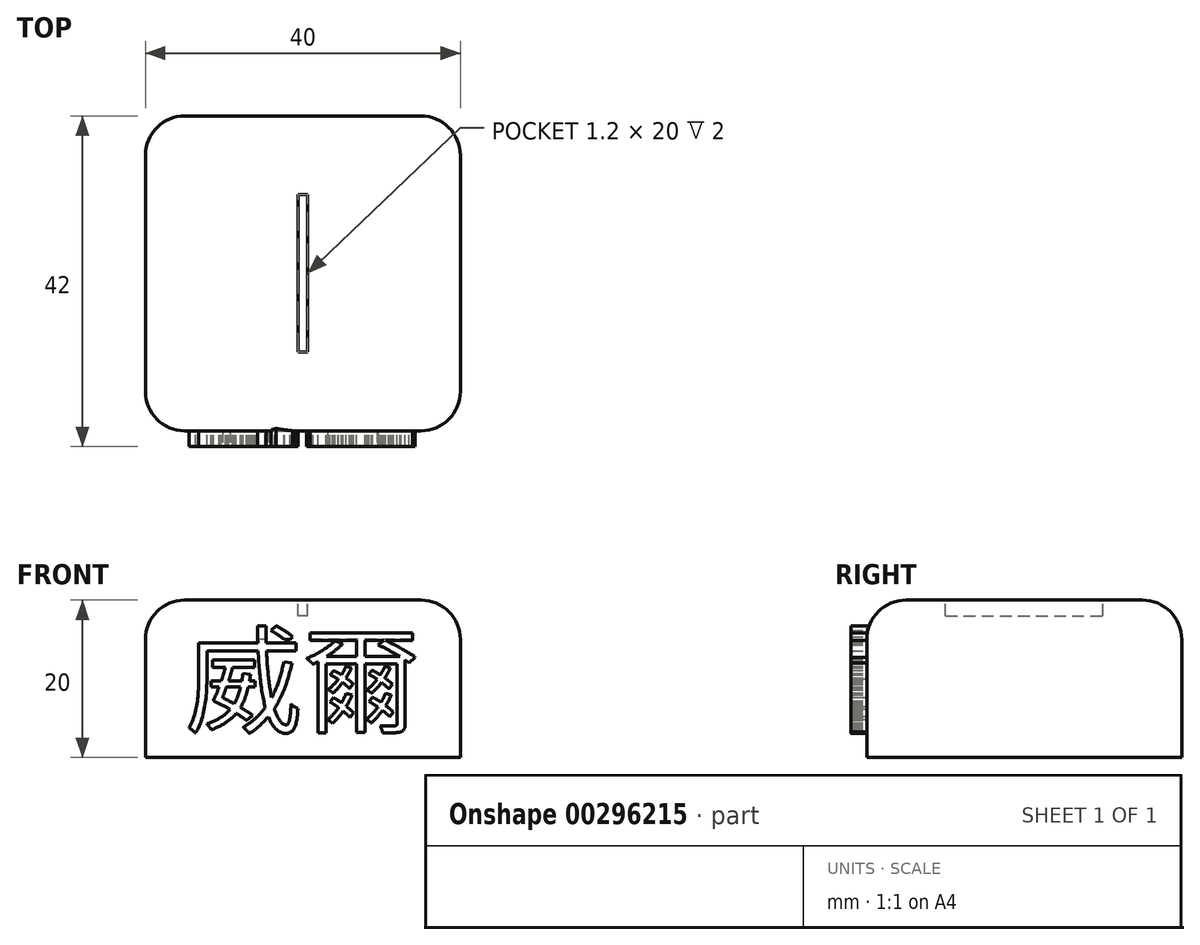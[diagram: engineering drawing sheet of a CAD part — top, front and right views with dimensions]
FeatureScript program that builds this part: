
annotation { "Feature Type Name" : "Feature", "Feature Type Description" : "" }
export const myFeature = defineFeature(function(context is Context, id is Id, definition is map)
    precondition{}
    {
        {
            var Q0;
            Q0=qCreatedBy(makeId("Top.planeOp"),FACE);
            var sketch = newSketch(context, id + "F0", { "sketchPlane" : qUnion([Q0])});
            skLineSegment(sketch, "E0.bottom", {"start": v(20, -20) * mm, "end": v(-20, -20) * mm});
            skLineSegment(sketch, "E0.top", {"start": v(20, 20) * mm, "end": v(-20, 20) * mm});
            skLineSegment(sketch, "E0.left", {"start": v(20, -20) * mm, "end": v(20, 20) * mm});
            skLineSegment(sketch, "E0.right", {"start": v(-20, -20) * mm, "end": v(-20, 20) * mm});
            skPoint(sketch, "E0.middle", {"position": v(0, 0) * mm});
            skLineSegment(sketch, "E1.bottom", {"start": v(0.6, -10) * mm, "end": v(-0.6, -10) * mm});
            skLineSegment(sketch, "E1.top", {"start": v(0.6, 10) * mm, "end": v(-0.6, 10) * mm});
            skLineSegment(sketch, "E1.left", {"start": v(0.6, -10) * mm, "end": v(0.6, 10) * mm});
            skLineSegment(sketch, "E1.right", {"start": v(-0.6, -10) * mm, "end": v(-0.6, 10) * mm});
            skSolve(sketch);
        }
        {
            var Q0;
            Q0=makeQuery(id+"F0.imprint","IMPRINT",FACE,{"disambiguationData":[TD([[makeQuery(id+"F0.imprint","IMPRINT",EDGE,{"derivedFrom":sQuery(id+"F0.wireOp",EDGE,"E0.bottom")}),-1.0]])]});
            var Q1;
            Q1=makeQuery(id+"F0.imprint","IMPRINT",FACE,{"disambiguationData":[TD([[makeQuery(id+"F0.imprint","IMPRINT",EDGE,{"derivedFrom":sQuery(id+"F0.wireOp",EDGE,"E1.bottom")}),-1.0]])]});
            extrude(context, id + "F1", {"entities" : qUnion([Q0, Q1]), "oppositeDirection" : true, "depth" : 20 * mm});
        }
        {
            var Q0;
            Q0=makeQuery(id+"F0.imprint","IMPRINT",FACE,{"disambiguationData":[TD([[makeQuery(id+"F0.imprint","IMPRINT",EDGE,{"derivedFrom":sQuery(id+"F0.wireOp",EDGE,"E1.bottom")}),-1.0]])]});
            extrude(context, id + "F2", {"entities" : qUnion([Q0]), "operationType" : NewBodyOperationType.REMOVE, "oppositeDirection" : true, "depth" : 2 * mm});
        }
        {
            var Q0;
            Q0=makeQuery(id+"F2.boolean.opBoolean","COPY",EDGE,{"derivedFrom":makeQuery(id+"F2.opExtrude","CAP_EDGE",EDGE,{"disambiguationData":[OSD([sQuery(id+"F0.wireOp",EDGE,"E1.left")])],"isStart":true})});
            var Q1;
            Q1=makeQuery(id+"F2.boolean.opBoolean","COPY",EDGE,{"derivedFrom":makeQuery(id+"F2.opExtrude","CAP_EDGE",EDGE,{"disambiguationData":[OSD([sQuery(id+"F0.wireOp",EDGE,"E1.right")])],"isStart":true})});
            var Q2;
            Q2=makeQuery(id+"F1.opExtrude","SWEPT_EDGE",EDGE,{"disambiguationData":[OSD([sQuery(id+"F0.wireOp",EDGE,"E0.bottom"),sQuery(id+"F0.wireOp",EDGE,"E0.left")])]});
            var Q3;
            Q3=makeQuery(id+"F1.opExtrude","SWEPT_EDGE",EDGE,{"disambiguationData":[OSD([sQuery(id+"F0.wireOp",EDGE,"E0.top"),sQuery(id+"F0.wireOp",EDGE,"E0.left")])]});
            var Q4;
            Q4=makeQuery(id+"F1.opExtrude","CAP_EDGE",EDGE,{"disambiguationData":[OSD([sQuery(id+"F0.wireOp",EDGE,"E0.left")])],"isStart":true});
            var Q5;
            Q5=makeQuery(id+"F1.opExtrude","SWEPT_EDGE",EDGE,{"disambiguationData":[OSD([sQuery(id+"F0.wireOp",EDGE,"E0.bottom"),sQuery(id+"F0.wireOp",EDGE,"E0.right")])]});
            var Q6;
            Q6=makeQuery(id+"F1.opExtrude","SWEPT_EDGE",EDGE,{"disambiguationData":[OSD([sQuery(id+"F0.wireOp",EDGE,"E0.top"),sQuery(id+"F0.wireOp",EDGE,"E0.right")])]});
            var Q7;
            Q7=makeQuery(id+"F1.opExtrude","CAP_EDGE",EDGE,{"disambiguationData":[OSD([sQuery(id+"F0.wireOp",EDGE,"E0.top")])],"isStart":true});
            var Q8;
            Q8=makeQuery(id+"F1.opExtrude","CAP_EDGE",EDGE,{"disambiguationData":[OSD([sQuery(id+"F0.wireOp",EDGE,"E0.right")])],"isStart":true});
            var Q9;
            Q9=makeQuery(id+"F1.opExtrude","CAP_EDGE",EDGE,{"disambiguationData":[OSD([sQuery(id+"F0.wireOp",EDGE,"E0.bottom")])],"isStart":true});
            fillet(context, id + "F3", {"entities" : qUnion([Q0, Q1, Q2, Q3, Q4, Q5, Q6, Q7, Q8, Q9]), "radius" : 5 * mm, "tangentPropagation" : true, "allowEdgeOverflow" : false});
        }
        {
            var Q0;
            Q0=makeQuery(id+"F1.opExtrude","SWEPT_FACE",FACE,{"disambiguationData":[OSD([sQuery(id+"F0.wireOp",EDGE,"E0.bottom")])]});
            var sketch = newSketch(context, id + "F4", { "sketchPlane" : qUnion([Q0])});
            skText(sketch, "E2", { "text": "威爾", "fontName": "NotoSansCJKtc-Regular.otf"});
            const initialGuessF4  = {"E2": [-0.015, -0.01575, 1, 0, 0.01075]};
            skSetInitialGuess(sketch, initialGuessF4);
            skSolve(sketch);
        }
        {
            var Q0;
            Q0=makeQuery(id+"F4.imprint","IMPRINT",FACE,{"disambiguationData":[TD([[makeQuery(id+"F4.imprint","IMPRINT",EDGE,{"derivedFrom":sQuery(id+"F4.wireOp",EDGE,"E2.sketch_text.stroke-34")}),1.0]])]});
            var Q1;
            {var subQ0=sQuery(id+"F4.wireOp",EDGE,"E2.sketch_text.stroke-40");Q1=makeQuery(id+"F4.imprint","IMPRINT",FACE,{"disambiguationData":[TD([[makeQuery(id+"F4.imprint","IMPRINT",EDGE,{"derivedFrom":subQ0}),1.0]])]});}
            var Q2;
            {var subQ7=sQuery(id+"F4.wireOp",EDGE,"E2.sketch_text.stroke-0");Q2=makeQuery(id+"F4.imprint","IMPRINT",FACE,{"disambiguationData":[TD([[makeQuery(id+"F4.imprint","IMPRINT",EDGE,{"derivedFrom":subQ7}),1.0]])]});}
            var Q3;
            Q3=makeQuery(id+"F4.imprint","IMPRINT",FACE,{"disambiguationData":[TD([[makeQuery(id+"F4.imprint","IMPRINT",EDGE,{"derivedFrom":sQuery(id+"F4.wireOp",EDGE,"E2.sketch_text.stroke-4")}),1.0]])]});
            var Q4;
            {var subQ0=sQuery(id+"F4.wireOp",EDGE,"E2.sketch_text.stroke-116");Q4=makeQuery(id+"F4.imprint","IMPRINT",FACE,{"disambiguationData":[TD([[makeQuery(id+"F4.imprint","IMPRINT",EDGE,{"derivedFrom":subQ0}),1.0]])]});}
            var Q5;
            Q5=makeQuery(id+"F4.imprint","IMPRINT",FACE,{"disambiguationData":[TD([[makeQuery(id+"F4.imprint","IMPRINT",EDGE,{"derivedFrom":sQuery(id+"F4.wireOp",EDGE,"E2.sketch_text.stroke-108")}),1.0]])]});
            var Q6;
            Q6=makeQuery(id+"F4.imprint","IMPRINT",FACE,{"disambiguationData":[TD([[makeQuery(id+"F4.imprint","IMPRINT",EDGE,{"derivedFrom":sQuery(id+"F4.wireOp",EDGE,"E2.sketch_text.stroke-72")}),1.0]])]});
            var Q7;
            Q7=makeQuery(id+"F4.imprint","IMPRINT",FACE,{"disambiguationData":[TD([[makeQuery(id+"F4.imprint","IMPRINT",EDGE,{"derivedFrom":sQuery(id+"F4.wireOp",EDGE,"E2.sketch_text.stroke-96")}),1.0]])]});
            var Q8;
            Q8=makeQuery(id+"F4.imprint","IMPRINT",FACE,{"disambiguationData":[TD([[makeQuery(id+"F4.imprint","IMPRINT",EDGE,{"derivedFrom":sQuery(id+"F4.wireOp",EDGE,"E2.sketch_text.stroke-84")}),1.0]])]});
            var Q9;
            Q9=makeQuery(id+"F4.imprint","IMPRINT",FACE,{"disambiguationData":[TD([[makeQuery(id+"F4.imprint","IMPRINT",EDGE,{"derivedFrom":sQuery(id+"F4.wireOp",EDGE,"E2.sketch_text.stroke-60")}),1.0]])]});
            extrude(context, id + "F5", {"entities" : qUnion([Q0, Q1, Q2, Q3, Q4, Q5, Q6, Q7, Q8, Q9]), "operationType" : NewBodyOperationType.ADD, "depth" : 2 * mm});
        }
        {
            var Q0;
            Q0=makeQuery(id+"F5.opExtrude","CAP_FACE",FACE,{"disambiguationData":[OSD([sQuery(id+"F0.wireOp",EDGE,"E0.bottom"),sQuery(id+"F4.wireOp",EDGE,"E2.sketch_text.stroke-0"),sQuery(id+"F4.wireOp",EDGE,"E2.sketch_text.stroke-1"),sQuery(id+"F4.wireOp",EDGE,"E2.sketch_text.stroke-2"),sQuery(id+"F4.wireOp",EDGE,"E2.sketch_text.stroke-3")])],"isStart":false});
            extrude(context, id + "F6", {"entities" : qUnion([Q0]), "operationType" : NewBodyOperationType.ADD, "oppositeDirection" : true, "depth" : 3 * mm});
        }
    });
